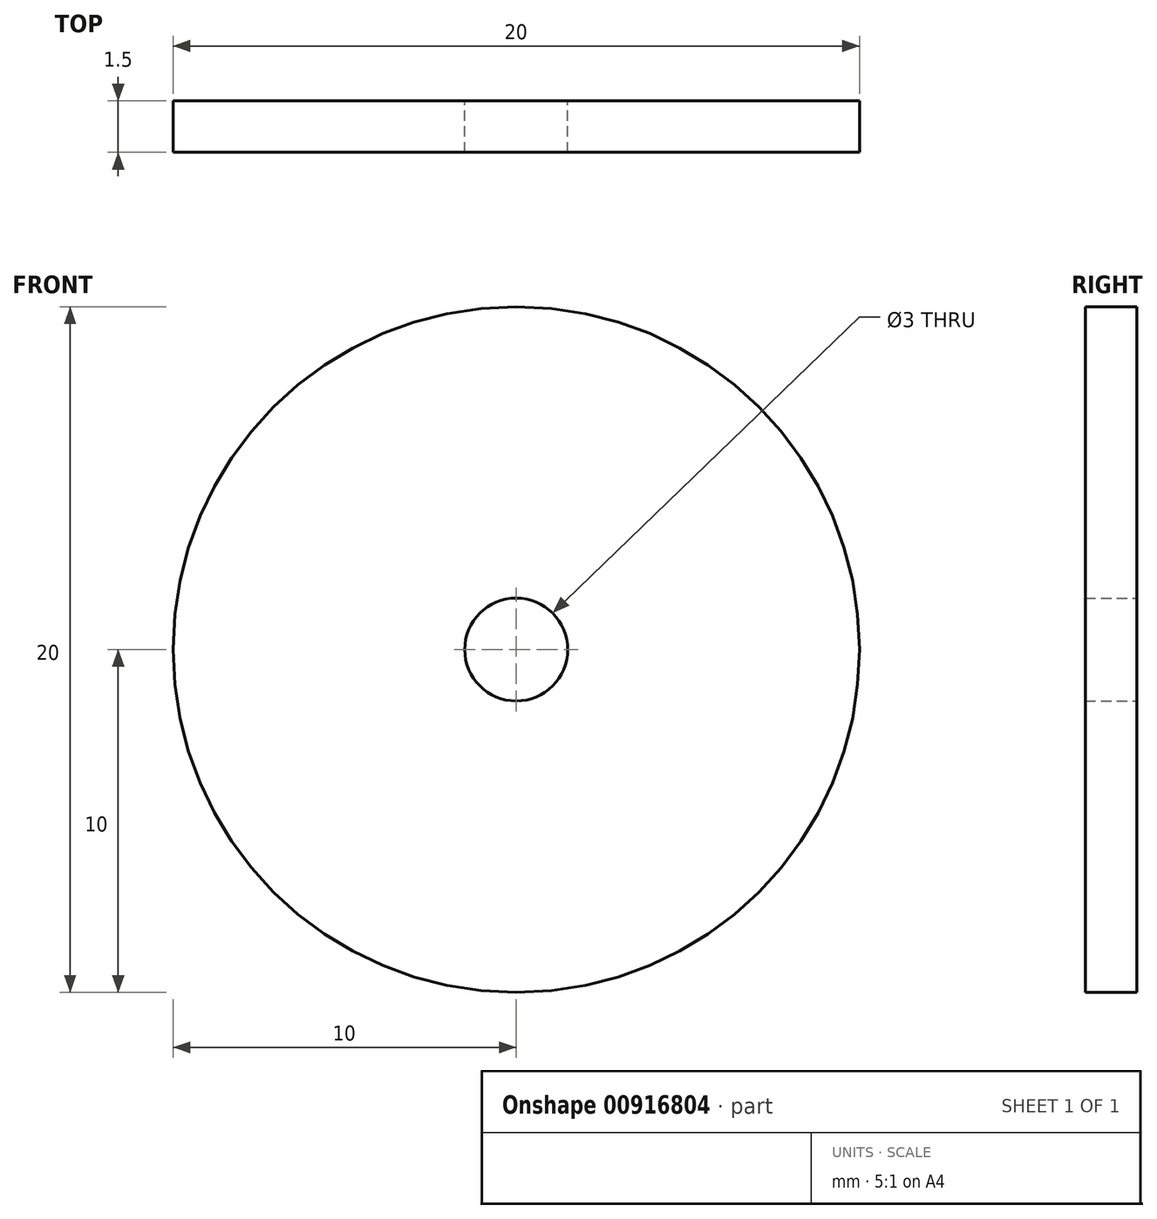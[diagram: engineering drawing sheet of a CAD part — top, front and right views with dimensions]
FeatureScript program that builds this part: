
annotation { "Feature Type Name" : "Feature", "Feature Type Description" : "" }
export const myFeature = defineFeature(function(context is Context, id is Id, definition is map)
    precondition{}
    {
        {
            var Q0;
            Q0=qCreatedBy(makeId("Front.planeOp"),FACE);
            var sketch = newSketch(context, id + "F0", { "sketchPlane" : qUnion([Q0])});
            skCircle(sketch, "E0", {"center": v(0, 0) * mm, "radius": 10 * mm});
            skCircle(sketch, "E1", {"center": v(0, 0) * mm, "radius": 1.5 * mm});
            skSolve(sketch);
        }
        {
            var Q0;
            Q0=makeQuery(id+"F0.imprint","IMPRINT",FACE,{"disambiguationData":[TD([[makeQuery(id+"F0.imprint","IMPRINT",EDGE,{"derivedFrom":sQuery(id+"F0.wireOp",EDGE,"E0")}),1.0]])]});
            extrude(context, id + "F1", {"entities" : qUnion([Q0]), "depth" : 1.5 * mm, "offsetDistance" : 25 * mm});
        }
    });
